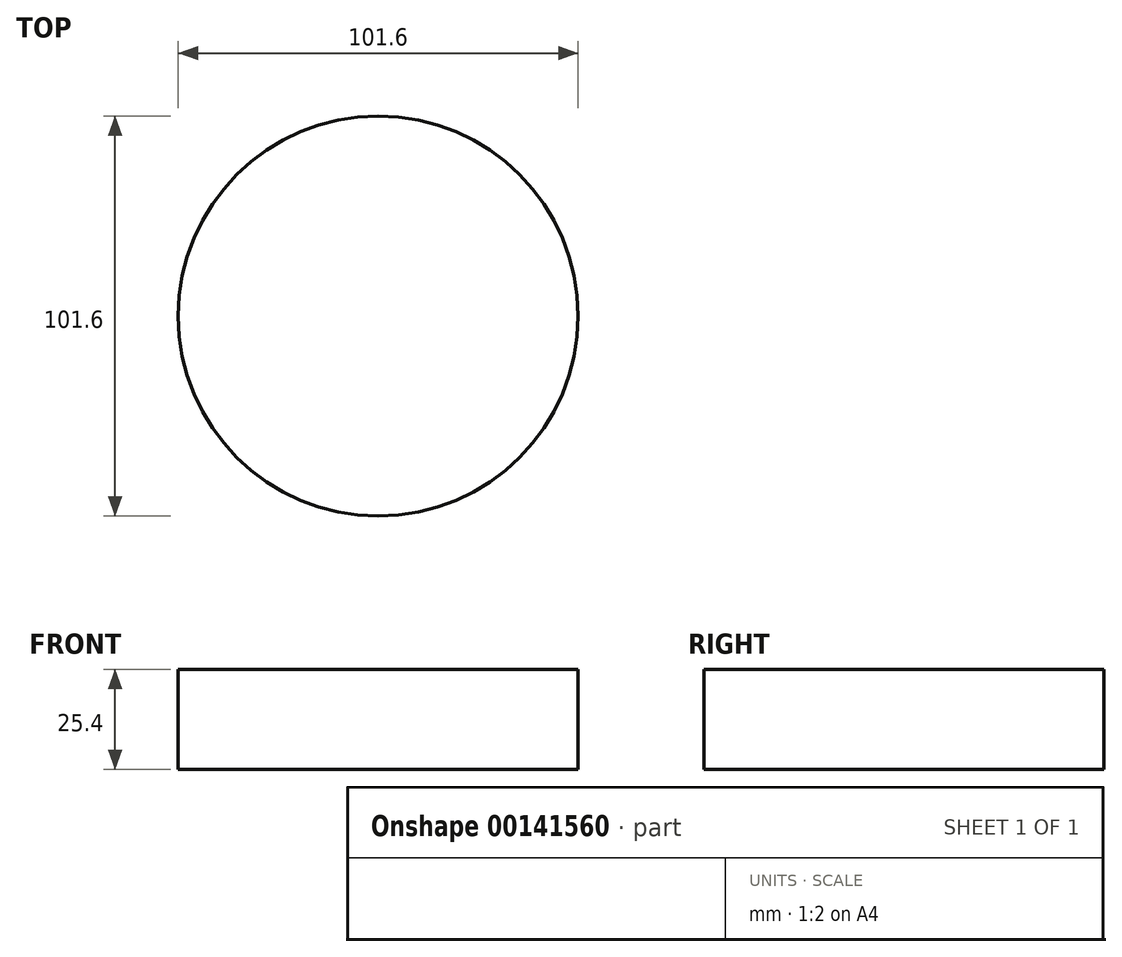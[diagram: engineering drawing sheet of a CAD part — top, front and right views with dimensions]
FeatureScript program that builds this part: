
annotation { "Feature Type Name" : "Feature", "Feature Type Description" : "" }
export const myFeature = defineFeature(function(context is Context, id is Id, definition is map)
    precondition{}
    {
        {
            var Q0;
            Q0=qCreatedBy(makeId("Top.planeOp"),FACE);
            var sketch = newSketch(context, id + "F0", { "sketchPlane" : qUnion([Q0])});
            skCircle(sketch, "E0", {"center": v(0, 0) * mm, "radius": 50.8 * mm});
            skSolve(sketch);
        }
        {
            var Q0;
            Q0 = qSketchRegion(id + "F0", true);
            var Q1;
            Q1=makeQuery(id+"F0.imprint","IMPRINT",FACE,{"disambiguationData":[TD([[makeQuery(id+"F0.imprint","IMPRINT",EDGE,{"derivedFrom":sQuery(id+"F0.wireOp",EDGE,"E0")}),1.0]])]});
            extrude(context, id + "F1", {"entities" : qUnion([Q0, Q1]), "endBound" : BoundingType.SYMMETRIC, "oppositeDirection" : true, "depth" : 25.4 * mm});
        }
    });
